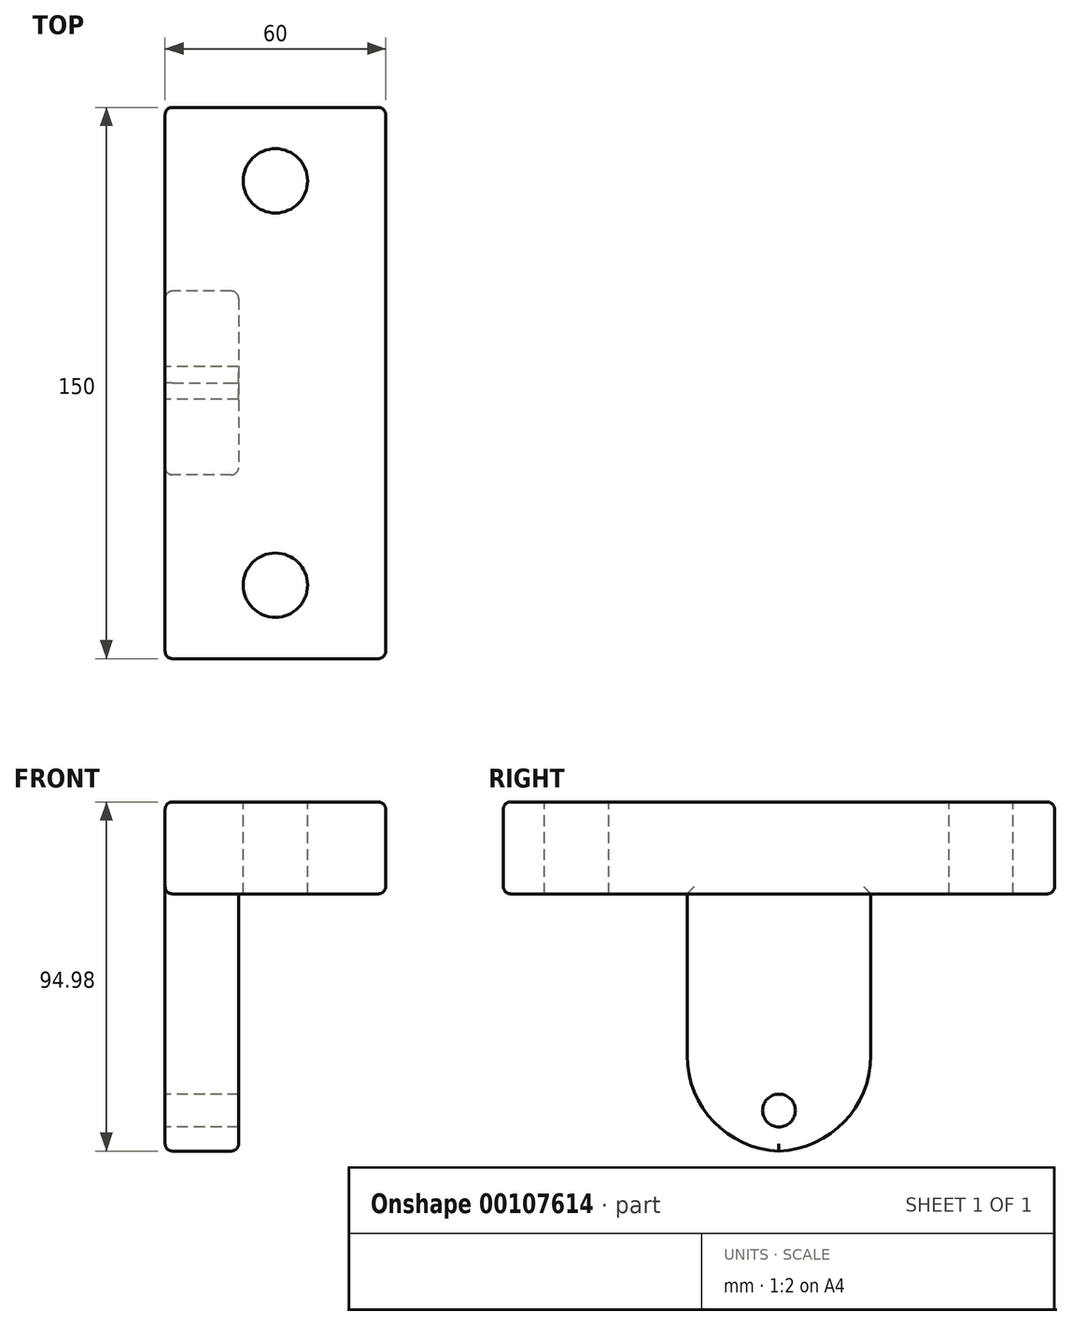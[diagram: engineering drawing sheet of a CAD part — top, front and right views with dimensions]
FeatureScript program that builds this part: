
annotation { "Feature Type Name" : "Feature", "Feature Type Description" : "" }
export const myFeature = defineFeature(function(context is Context, id is Id, definition is map)
    precondition{}
    {
        {
            var Q0;
            Q0=qCreatedBy(makeId("Top.planeOp"),FACE);
            var sketch = newSketch(context, id + "F0", { "sketchPlane" : qUnion([Q0])});
            skLineSegment(sketch, "E0.bottom", {"start": v(30, -75) * mm, "end": v(-30, -75) * mm});
            skLineSegment(sketch, "E0.top", {"start": v(30, 75) * mm, "end": v(-30, 75) * mm});
            skLineSegment(sketch, "E0.left", {"start": v(30, -75) * mm, "end": v(30, 75) * mm});
            skLineSegment(sketch, "E0.right", {"start": v(-30, -75) * mm, "end": v(-30, 75) * mm});
            skPoint(sketch, "E0.middle", {"position": v(0, 0) * mm});
            skSolve(sketch);
        }
        {
            var Q0;
            Q0 = qSketchRegion(id + "F0", true);
            extrude(context, id + "F1", {"entities" : qUnion([Q0]), "depth" : 25 * mm});
        }
        {
            var Q0;
            Q0=makeQuery(id+"F1.opExtrude","CAP_FACE",FACE,{"disambiguationData":[OSD([sQuery(id+"F0.wireOp",EDGE,"E0.bottom"),sQuery(id+"F0.wireOp",EDGE,"E0.top"),sQuery(id+"F0.wireOp",EDGE,"E0.left"),sQuery(id+"F0.wireOp",EDGE,"E0.right")])],"isStart":false});
            var sketch = newSketch(context, id + "F2", { "sketchPlane" : qUnion([Q0])});
            skCircle(sketch, "E1", {"center": v(0, 55) * mm, "radius": 8.75 * mm});
            skCircle(sketch, "E2", {"center": v(0, -55) * mm, "radius": 8.75 * mm});
            skLineSegment(sketch, "E3.bottom", {"start": v(-10, 25) * mm, "end": v(-30, 25) * mm});
            skLineSegment(sketch, "E3.top", {"start": v(-10, -25) * mm, "end": v(-30, -25) * mm});
            skLineSegment(sketch, "E3.left", {"start": v(-10, 25) * mm, "end": v(-10, -25) * mm});
            skLineSegment(sketch, "E3.right", {"start": v(-30, 25) * mm, "end": v(-30, -25) * mm});
            skPoint(sketch, "E3.middle", {"position": v(-20, 0) * mm});
            skSolve(sketch);
        }
        {
            var Q0;
            Q0 = qSketchRegion(id + "F2", true);
            extrude(context, id + "F3", {"entities" : qUnion([Q0]), "operationType" : NewBodyOperationType.REMOVE, "oppositeDirection" : true, "depth" : 25 * mm});
        }
        {
            var Q0;
            Q0=makeQuery(id+"F2.imprint","IMPRINT",FACE,{"disambiguationData":[TD([[makeQuery(id+"F2.imprint","IMPRINT",EDGE,{"derivedFrom":sQuery(id+"F2.wireOp",EDGE,"E3.bottom")}),1.0]])]});
            extrude(context, id + "F4", {"entities" : qUnion([Q0]), "operationType" : NewBodyOperationType.ADD, "oppositeDirection" : true, "depth" : 70 * mm});
        }
        {
            var Q0;
            {var subQ0=sQuery(id+"F0.wireOp",EDGE,"E0.right");var subQ1=sQuery(id+"F0.wireOp",EDGE,"E0.top");Q0=makeQuery(id+"F3.boolean.opBoolean","SPLIT",EDGE,{"disambiguationData":[TD([makeQuery(id+"F1.opExtrude","SWEPT_FACE",FACE,{"disambiguationData":[OSD([subQ1])]})])],"derivedFrom":makeQuery(id+"F1.opExtrude","CAP_EDGE",EDGE,{"disambiguationData":[OSD([subQ0])],"isStart":true})});}
            var Q1;
            Q1=makeQuery(id+"F4.opExtrude","SWEPT_EDGE",EDGE,{"disambiguationData":[OSD([sQuery(id+"F0.wireOp",EDGE,"E0.right"),sQuery(id+"F2.wireOp",EDGE,"E3.bottom"),sQuery(id+"F2.wireOp",EDGE,"E3.right")])]});
            var Q2;
            Q2=makeQuery(id+"F1.opExtrude","SWEPT_FACE",FACE,{"disambiguationData":[OSD([sQuery(id+"F0.wireOp",EDGE,"E0.top")])]});
            var Q3;
            Q3=makeQuery(id+"F4.opExtrude","SWEPT_EDGE",EDGE,{"disambiguationData":[OSD([sQuery(id+"F2.wireOp",EDGE,"E3.bottom"),sQuery(id+"F2.wireOp",EDGE,"E3.left")])]});
            var Q4;
            {var subQ0=sQuery(id+"F0.wireOp",EDGE,"E0.right");var subQ1=sQuery(id+"F0.wireOp",EDGE,"E0.top");var subQ2=sQuery(id+"F0.wireOp",EDGE,"E0.bottom");var subQ5=makeQuery(id+"F1.opExtrude","CAP_EDGE",EDGE,{"disambiguationData":[OSD([subQ0])],"isStart":false});Q4=makeQuery(id+"F4.boolean.opBoolean","MERGE",EDGE,{"derivedFrom":[makeQuery(id+"F3.boolean.opBoolean","SPLIT",EDGE,{"disambiguationData":[TD([makeQuery(id+"F1.opExtrude","SWEPT_FACE",FACE,{"disambiguationData":[OSD([subQ2])]})])],"derivedFrom":subQ5}),makeQuery(id+"F3.boolean.opBoolean","SPLIT",EDGE,{"disambiguationData":[TD([makeQuery(id+"F1.opExtrude","SWEPT_FACE",FACE,{"disambiguationData":[OSD([subQ1])]})])],"derivedFrom":subQ5}),makeQuery(id+"F4.opExtrude","CAP_EDGE",EDGE,{"disambiguationData":[OSD([sQuery(id+"F2.wireOp",EDGE,"E3.right")])],"isStart":true})]});}
            var Q5;
            {var subQ0=sQuery(id+"F0.wireOp",EDGE,"E0.bottom");var subQ1=sQuery(id+"F0.wireOp",EDGE,"E0.right");Q5=makeQuery(id+"F3.boolean.opBoolean","SPLIT",EDGE,{"disambiguationData":[TD([makeQuery(id+"F1.opExtrude","SWEPT_FACE",FACE,{"disambiguationData":[OSD([subQ0])]})])],"derivedFrom":makeQuery(id+"F1.opExtrude","CAP_EDGE",EDGE,{"disambiguationData":[OSD([subQ1])],"isStart":true})});}
            var Q6;
            Q6=makeQuery(id+"F4.opExtrude","SWEPT_EDGE",EDGE,{"disambiguationData":[OSD([sQuery(id+"F0.wireOp",EDGE,"E0.right"),sQuery(id+"F2.wireOp",EDGE,"E3.top"),sQuery(id+"F2.wireOp",EDGE,"E3.right")])]});
            var Q7;
            Q7=makeQuery(id+"F1.opExtrude","CAP_EDGE",EDGE,{"disambiguationData":[OSD([sQuery(id+"F0.wireOp",EDGE,"E0.left")])],"isStart":true});
            var Q8;
            Q8=makeQuery(id+"F1.opExtrude","CAP_EDGE",EDGE,{"disambiguationData":[OSD([sQuery(id+"F0.wireOp",EDGE,"E0.left")])],"isStart":false});
            var Q9;
            Q9=makeQuery(id+"F1.opExtrude","CAP_EDGE",EDGE,{"disambiguationData":[OSD([sQuery(id+"F0.wireOp",EDGE,"E0.bottom")])],"isStart":false});
            var Q10;
            Q10=makeQuery(id+"F1.opExtrude","SWEPT_EDGE",EDGE,{"disambiguationData":[OSD([sQuery(id+"F0.wireOp",EDGE,"E0.bottom"),sQuery(id+"F0.wireOp",EDGE,"E0.right")])]});
            var Q11;
            Q11=makeQuery(id+"F1.opExtrude","SWEPT_EDGE",EDGE,{"disambiguationData":[OSD([sQuery(id+"F0.wireOp",EDGE,"E0.bottom"),sQuery(id+"F0.wireOp",EDGE,"E0.left")])]});
            var Q12;
            Q12=makeQuery(id+"F1.opExtrude","SWEPT_FACE",FACE,{"disambiguationData":[OSD([sQuery(id+"F0.wireOp",EDGE,"E0.bottom")])]});
            var Q13;
            Q13=makeQuery(id+"F4.opExtrude","SWEPT_EDGE",EDGE,{"disambiguationData":[OSD([sQuery(id+"F2.wireOp",EDGE,"E3.top"),sQuery(id+"F2.wireOp",EDGE,"E3.left")])]});
            fillet(context, id + "F5", {"entities" : qUnion([Q0, Q1, Q2, Q3, Q4, Q5, Q6, Q7, Q8, Q9, Q10, Q11, Q12, Q13]), "radius" : 2 * mm, "tangentPropagation" : true, "allowEdgeOverflow" : false});
        }
        {
            var Q0;
            Q0=makeQuery(id+"F4.opExtrude","CAP_FACE",FACE,{"disambiguationData":[OSD([sQuery(id+"F2.wireOp",EDGE,"E3.bottom"),sQuery(id+"F2.wireOp",EDGE,"E3.top"),sQuery(id+"F2.wireOp",EDGE,"E3.left"),sQuery(id+"F2.wireOp",EDGE,"E3.right")])],"isStart":false});
            var sketch = newSketch(context, id + "F6", { "sketchPlane" : qUnion([Q0])});
            skSolve(sketch);
        }
        {
            var Q0;
            {var subQ3=sQuery(id+"F2.wireOp",EDGE,"E3.bottom");Q0=makeQuery(id+"F6.imprint","IMPRINT",FACE,{"disambiguationData":[TD([[makeQuery(id+"F6.imprint","IMPRINT",EDGE,{"derivedFrom":makeQuery(id+"F4.opExtrude","CAP_EDGE",EDGE,{"disambiguationData":[OSD([subQ3])],"isStart":false})}),-1.0]])]});}
            extrude(context, id + "F7", {"entities" : qUnion([Q0]), "operationType" : NewBodyOperationType.ADD, "depth" : 25 * mm});
        }
        {
            var Q0;
            Q0=makeQuery(id+"F7.opExtrude","CAP_EDGE",EDGE,{"disambiguationData":[OSD([sQuery(id+"F2.wireOp",EDGE,"E3.top")])],"isStart":false});
            var Q1;
            Q1=makeQuery(id+"F7.opExtrude","CAP_EDGE",EDGE,{"disambiguationData":[OSD([sQuery(id+"F2.wireOp",EDGE,"E3.bottom")])],"isStart":false});
            fillet(context, id + "F8", {"entities" : qUnion([Q0, Q1]), "radius" : 26 * mm, "allowEdgeOverflow" : false});
        }
        {
            var Q0;
            {var subQ0=sQuery(id+"F2.wireOp",EDGE,"E3.right");var subQ1=sQuery(id+"F0.wireOp",EDGE,"E0.right");var subQ3=sQuery(id+"F0.wireOp",EDGE,"E0.top");var subQ4=sQuery(id+"F0.wireOp",EDGE,"E0.bottom");var subQ7=makeQuery(id+"F1.opExtrude","SWEPT_FACE",FACE,{"disambiguationData":[OSD([subQ1])]});Q0=makeQuery(id+"F7.boolean.opBoolean","MERGE",FACE,{"derivedFrom":[makeQuery(id+"F4.boolean.opBoolean","MERGE",FACE,{"derivedFrom":[makeQuery(id+"F3.boolean.opBoolean","SPLIT",FACE,{"disambiguationData":[TD([makeQuery(id+"F1.opExtrude","SWEPT_FACE",FACE,{"disambiguationData":[OSD([subQ4])]})])],"derivedFrom":subQ7}),makeQuery(id+"F3.boolean.opBoolean","SPLIT",FACE,{"disambiguationData":[TD([makeQuery(id+"F1.opExtrude","SWEPT_FACE",FACE,{"disambiguationData":[OSD([subQ3])]})])],"derivedFrom":subQ7}),makeQuery(id+"F4.opExtrude","SWEPT_FACE",FACE,{"disambiguationData":[OSD([subQ0])]})]}),makeQuery(id+"F7.opExtrude","SWEPT_FACE",FACE,{"disambiguationData":[OSD([subQ0])]})]});}
            var sketch = newSketch(context, id + "F9", { "sketchPlane" : qUnion([Q0])});
            skCircle(sketch, "E4", {"center": v(0, -58.95) * mm, "radius": 4.46 * mm});
            skSolve(sketch);
        }
        {
            var Q0;
            Q0 = qSketchRegion(id + "F9", true);
            extrude(context, id + "F10", {"entities" : qUnion([Q0]), "operationType" : NewBodyOperationType.REMOVE, "oppositeDirection" : true, "depth" : 25 * mm});
        }
        {
            var Q0;
            {var subQ0=sQuery(id+"F2.wireOp",EDGE,"E3.left");Q0=makeQuery(id+"F8.opFillet","BLEND_EDGE",EDGE,{"blendedFrom":[makeQuery(id+"F7.opExtrude","CAP_EDGE",EDGE,{"disambiguationData":[OSD([sQuery(id+"F2.wireOp",EDGE,"E3.bottom")])],"isStart":false}),makeQuery(id+"F7.boolean.opBoolean","MERGE",FACE,{"derivedFrom":[makeQuery(id+"F4.opExtrude","SWEPT_FACE",FACE,{"disambiguationData":[OSD([subQ0])]}),makeQuery(id+"F7.opExtrude","SWEPT_FACE",FACE,{"disambiguationData":[OSD([subQ0])]})]})],"blendedInto":[makeQuery(id+"F7.boolean.opBoolean","MERGE",FACE,{"derivedFrom":[makeQuery(id+"F4.opExtrude","SWEPT_FACE",FACE,{"disambiguationData":[OSD([subQ0])]}),makeQuery(id+"F7.opExtrude","SWEPT_FACE",FACE,{"disambiguationData":[OSD([subQ0])]})]})]});}
            var Q1;
            {var subQ0=sQuery(id+"F2.wireOp",EDGE,"E3.left");Q1=makeQuery(id+"F8.opFillet","BLEND_EDGE",EDGE,{"blendedFrom":[makeQuery(id+"F7.opExtrude","CAP_EDGE",EDGE,{"disambiguationData":[OSD([sQuery(id+"F2.wireOp",EDGE,"E3.top")])],"isStart":false}),makeQuery(id+"F7.boolean.opBoolean","MERGE",FACE,{"derivedFrom":[makeQuery(id+"F4.opExtrude","SWEPT_FACE",FACE,{"disambiguationData":[OSD([subQ0])]}),makeQuery(id+"F7.opExtrude","SWEPT_FACE",FACE,{"disambiguationData":[OSD([subQ0])]})]})],"blendedInto":[makeQuery(id+"F7.boolean.opBoolean","MERGE",FACE,{"derivedFrom":[makeQuery(id+"F4.opExtrude","SWEPT_FACE",FACE,{"disambiguationData":[OSD([subQ0])]}),makeQuery(id+"F7.opExtrude","SWEPT_FACE",FACE,{"disambiguationData":[OSD([subQ0])]})]})]});}
            var Q2;
            {var subQ0=sQuery(id+"F2.wireOp",EDGE,"E3.right");var subQ1=sQuery(id+"F0.wireOp",EDGE,"E0.right");var subQ3=sQuery(id+"F0.wireOp",EDGE,"E0.top");var subQ4=sQuery(id+"F0.wireOp",EDGE,"E0.bottom");var subQ7=makeQuery(id+"F1.opExtrude","SWEPT_FACE",FACE,{"disambiguationData":[OSD([subQ1])]});var subQ8=sQuery(id+"F2.wireOp",EDGE,"E3.top");Q2=makeQuery(id+"F8.opFillet","BLEND_EDGE",EDGE,{"blendedFrom":[makeQuery(id+"F7.opExtrude","CAP_EDGE",EDGE,{"disambiguationData":[OSD([subQ8])],"isStart":false}),makeQuery(id+"F7.boolean.opBoolean","MERGE",FACE,{"derivedFrom":[makeQuery(id+"F4.boolean.opBoolean","MERGE",FACE,{"derivedFrom":[makeQuery(id+"F3.boolean.opBoolean","SPLIT",FACE,{"disambiguationData":[TD([makeQuery(id+"F1.opExtrude","SWEPT_FACE",FACE,{"disambiguationData":[OSD([subQ4])]})])],"derivedFrom":subQ7}),makeQuery(id+"F3.boolean.opBoolean","SPLIT",FACE,{"disambiguationData":[TD([makeQuery(id+"F1.opExtrude","SWEPT_FACE",FACE,{"disambiguationData":[OSD([subQ3])]})])],"derivedFrom":subQ7}),makeQuery(id+"F4.opExtrude","SWEPT_FACE",FACE,{"disambiguationData":[OSD([subQ0])]})]}),makeQuery(id+"F7.opExtrude","SWEPT_FACE",FACE,{"disambiguationData":[OSD([subQ0])]})]})],"blendedInto":[makeQuery(id+"F7.boolean.opBoolean","MERGE",FACE,{"derivedFrom":[makeQuery(id+"F4.boolean.opBoolean","MERGE",FACE,{"derivedFrom":[makeQuery(id+"F3.boolean.opBoolean","SPLIT",FACE,{"disambiguationData":[TD([makeQuery(id+"F1.opExtrude","SWEPT_FACE",FACE,{"disambiguationData":[OSD([subQ4])]})])],"derivedFrom":subQ7}),makeQuery(id+"F3.boolean.opBoolean","SPLIT",FACE,{"disambiguationData":[TD([makeQuery(id+"F1.opExtrude","SWEPT_FACE",FACE,{"disambiguationData":[OSD([subQ3])]})])],"derivedFrom":subQ7}),makeQuery(id+"F4.opExtrude","SWEPT_FACE",FACE,{"disambiguationData":[OSD([subQ0])]})]}),makeQuery(id+"F7.opExtrude","SWEPT_FACE",FACE,{"disambiguationData":[OSD([subQ0])]})]})]});}
            var Q3;
            {var subQ0=sQuery(id+"F2.wireOp",EDGE,"E3.right");var subQ1=sQuery(id+"F0.wireOp",EDGE,"E0.right");var subQ3=sQuery(id+"F0.wireOp",EDGE,"E0.top");var subQ4=sQuery(id+"F0.wireOp",EDGE,"E0.bottom");var subQ7=sQuery(id+"F2.wireOp",EDGE,"E3.bottom");var subQ8=makeQuery(id+"F1.opExtrude","SWEPT_FACE",FACE,{"disambiguationData":[OSD([subQ1])]});Q3=makeQuery(id+"F8.opFillet","BLEND_EDGE",EDGE,{"blendedFrom":[makeQuery(id+"F7.opExtrude","CAP_EDGE",EDGE,{"disambiguationData":[OSD([subQ7])],"isStart":false}),makeQuery(id+"F7.boolean.opBoolean","MERGE",FACE,{"derivedFrom":[makeQuery(id+"F4.boolean.opBoolean","MERGE",FACE,{"derivedFrom":[makeQuery(id+"F3.boolean.opBoolean","SPLIT",FACE,{"disambiguationData":[TD([makeQuery(id+"F1.opExtrude","SWEPT_FACE",FACE,{"disambiguationData":[OSD([subQ4])]})])],"derivedFrom":subQ8}),makeQuery(id+"F3.boolean.opBoolean","SPLIT",FACE,{"disambiguationData":[TD([makeQuery(id+"F1.opExtrude","SWEPT_FACE",FACE,{"disambiguationData":[OSD([subQ3])]})])],"derivedFrom":subQ8}),makeQuery(id+"F4.opExtrude","SWEPT_FACE",FACE,{"disambiguationData":[OSD([subQ0])]})]}),makeQuery(id+"F7.opExtrude","SWEPT_FACE",FACE,{"disambiguationData":[OSD([subQ0])]})]})],"blendedInto":[makeQuery(id+"F7.boolean.opBoolean","MERGE",FACE,{"derivedFrom":[makeQuery(id+"F4.boolean.opBoolean","MERGE",FACE,{"derivedFrom":[makeQuery(id+"F3.boolean.opBoolean","SPLIT",FACE,{"disambiguationData":[TD([makeQuery(id+"F1.opExtrude","SWEPT_FACE",FACE,{"disambiguationData":[OSD([subQ4])]})])],"derivedFrom":subQ8}),makeQuery(id+"F3.boolean.opBoolean","SPLIT",FACE,{"disambiguationData":[TD([makeQuery(id+"F1.opExtrude","SWEPT_FACE",FACE,{"disambiguationData":[OSD([subQ3])]})])],"derivedFrom":subQ8}),makeQuery(id+"F4.opExtrude","SWEPT_FACE",FACE,{"disambiguationData":[OSD([subQ0])]})]}),makeQuery(id+"F7.opExtrude","SWEPT_FACE",FACE,{"disambiguationData":[OSD([subQ0])]})]})]});}
            fillet(context, id + "F11", {"entities" : qUnion([Q0, Q1, Q2, Q3]), "radius" : 2 * mm, "tangentPropagation" : true, "allowEdgeOverflow" : false});
        }
    });
